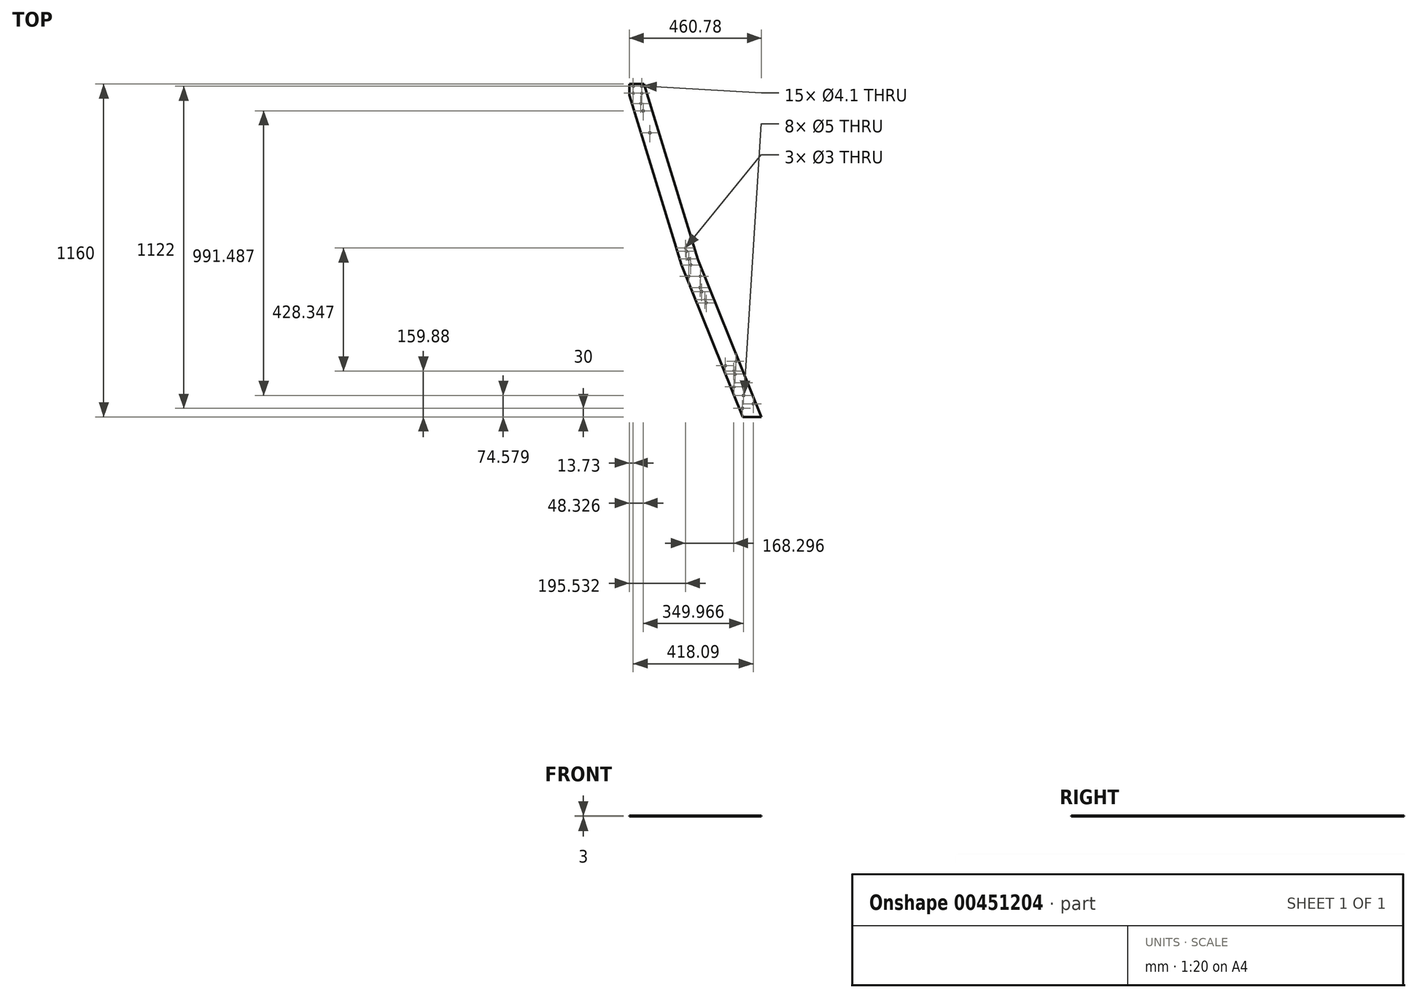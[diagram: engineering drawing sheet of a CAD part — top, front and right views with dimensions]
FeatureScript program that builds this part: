
annotation { "Feature Type Name" : "Feature", "Feature Type Description" : "" }
export const myFeature = defineFeature(function(context is Context, id is Id, definition is map)
    precondition{}
    {
        {
            var Q0;
            Q0=qCreatedBy(makeId("Top.planeOp"),FACE);
            var sketch = newSketch(context, id + "F0", { "sketchPlane" : qUnion([Q0])});
            skLineSegment(sketch, "E0", {"start": v(0, 0) * mm, "end": v(-64.71, 0) * mm});
            skLineSegment(sketch, "E1", {"start": v(-472.78, 1160) * mm, "end": v(-410, 1160) * mm});
            skLineSegment(sketch, "E2", {"start": v(-472.78, 1160) * mm, "end": v(-278.24, 528.5) * mm});
            skLineSegment(sketch, "E3", {"start": v(-278.24, 528.5) * mm, "end": v(-64.71, 0) * mm});
            skLineSegment(sketch, "E4", {"start": v(0, 0) * mm, "end": v(-221.65, 548.6) * mm});
            skLineSegment(sketch, "E5", {"start": v(-410, 1160) * mm, "end": v(-221.65, 548.6) * mm});
            skLineSegment(sketch, "E6", {"start": v(-32.36, 0) * mm, "end": v(-248.68, 535.42) * mm, "construction": true});
            skCircle(sketch, "E7", {"center": v(-208.58, 436.18) * mm, "radius": 2.5 * mm});
            skLineSegment(sketch, "E8", {"start": v(-202.7, 368.24) * mm, "end": v(-55.04, 2.75) * mm, "construction": true});
            skCircle(sketch, "E9", {"center": v(-66.05, 30) * mm, "radius": 2.05 * mm});
            skCircle(sketch, "E10", {"center": v(-96.02, 104.17) * mm, "radius": 2.05 * mm});
            skCircle(sketch, "E11", {"center": v(-125.98, 178.35) * mm, "radius": 2.05 * mm});
            skCircle(sketch, "E12.MirrorC", {"center": v(-28.96, 44.98) * mm, "radius": 2.05 * mm});
            skCircle(sketch, "E13.MirrorC", {"center": v(-58.93, 119.16) * mm, "radius": 2.05 * mm});
            skCircle(sketch, "E14.MirrorC", {"center": v(-88.9, 193.33) * mm, "radius": 2.05 * mm});
            skLineSegment(sketch, "E15", {"start": v(-125.98, 178.35) * mm, "end": v(-88.9, 193.33) * mm, "construction": true});
            skLineSegment(sketch, "E16", {"start": v(-66.05, 30) * mm, "end": v(-28.96, 44.98) * mm, "construction": true});
            skCircle(sketch, "E17", {"center": v(-62.49, 74.58) * mm, "radius": 2.5 * mm});
            skPoint(sketch, "E18", {"position": v(-92.46, 148.75) * mm});
            skCircle(sketch, "E19", {"center": v(-96.95, 159.88) * mm, "radius": 1.5 * mm});
            skCircle(sketch, "E20", {"center": v(-92.46, 148.75) * mm, "radius": 2.5 * mm});
            skCircle(sketch, "E21", {"center": v(-192.85, 397.24) * mm, "radius": 2.5 * mm});
            skCircle(sketch, "E22", {"center": v(-197.35, 408.37) * mm, "radius": 1.5 * mm});
            skCircle(sketch, "E23", {"center": v(-253.47, 550) * mm, "radius": 2.5 * mm});
            skLineSegment(sketch, "E24", {"start": v(-433.64, 1134.83) * mm, "end": v(-251.34, 543.08) * mm, "construction": true});
            skLineSegment(sketch, "E25", {"start": v(-278.24, 528.5) * mm, "end": v(-221.65, 548.6) * mm, "construction": true});
            skCircle(sketch, "E26", {"center": v(-412.45, 1066.07) * mm, "radius": 2.5 * mm});
            skCircle(sketch, "E27", {"center": v(-261.72, 576.76) * mm, "radius": 2.5 * mm});
            skCircle(sketch, "E28", {"center": v(-265.25, 588.23) * mm, "radius": 1.5 * mm});
            skCircle(sketch, "E29", {"center": v(-420.4, 1091.87) * mm, "radius": 2.05 * mm});
            skCircle(sketch, "E30", {"center": v(-388.9, 989.61) * mm, "radius": 2.5 * mm});
            skCircle(sketch, "E31", {"center": v(-246.25, 529.4) * mm, "radius": 2.05 * mm});
            skCircle(sketch, "E32", {"center": v(-214.4, 450.6) * mm, "radius": 2.05 * mm});
            skSolve(sketch);
        }
        {
            var Q0;
            Q0=qSketchRegion(id+"F0",true);
            extrude(context, id + "F1", {"entities" : qUnion([Q0]), "depth" : 3 * mm, "offsetDistance" : 25 * mm});
        }
        {
            var Q0;
            Q0=makeQuery(id+"F1.opExtrude","CAP_FACE",FACE,{"disambiguationData":[OSD([sQuery(id+"F0.wireOp",EDGE,"E0"),sQuery(id+"F0.wireOp",EDGE,"E1"),sQuery(id+"F0.wireOp",EDGE,"E2"),sQuery(id+"F0.wireOp",EDGE,"E3"),sQuery(id+"F0.wireOp",EDGE,"E4"),sQuery(id+"F0.wireOp",EDGE,"E5"),sQuery(id+"F0.wireOp",EDGE,"gJt8cwgu-VA7b-SDAH-htXG-uJ1Z7NdRgci2"),sQuery(id+"F0.wireOp",EDGE,"seKeo64r-ZTq0-B8et-10Xg-iBB15py0T0ax"),sQuery(id+"F0.wireOp",EDGE,"dKAoz8lV-Klpz-Zx3G-pcuS-yv6v6ew4PkVc")])],"isStart":false});
            var sketch = newSketch(context, id + "F2", { "sketchPlane" : qUnion([Q0])});
            skCircle(sketch, "E33", {"center": v(-252.94, 490) * mm, "radius": 2.05 * mm});
            skCircle(sketch, "E34", {"center": v(-212.94, 490) * mm, "radius": 2.05 * mm});
            skCircle(sketch, "E35", {"center": v(-447.05, 1152) * mm, "radius": 2.05 * mm});
            skCircle(sketch, "E36", {"center": v(-417.05, 1152) * mm, "radius": 2.05 * mm});
            skCircle(sketch, "E37", {"center": v(-447.05, 1128) * mm, "radius": 2.05 * mm});
            skCircle(sketch, "E38", {"center": v(-417.05, 1128) * mm, "radius": 2.05 * mm});
            skSolve(sketch);
        }
        {
            var Q0;
            Q0 = qSketchRegion(id + "F2", true);
            extrude(context, id + "F3", {"entities" : qUnion([Q0]), "operationType" : NewBodyOperationType.REMOVE, "oppositeDirection" : true, "depth" : 25 * mm, "offsetDistance" : 25 * mm});
        }
        {
            var Q0;
            Q0=makeQuery(id+"F1.opExtrude","CAP_FACE",FACE,{"disambiguationData":[OSD([sQuery(id+"F0.wireOp",EDGE,"E0"),sQuery(id+"F0.wireOp",EDGE,"E1"),sQuery(id+"F0.wireOp",EDGE,"E2"),sQuery(id+"F0.wireOp",EDGE,"E3"),sQuery(id+"F0.wireOp",EDGE,"E4"),sQuery(id+"F0.wireOp",EDGE,"E5"),sQuery(id+"F0.wireOp",EDGE,"E7"),sQuery(id+"F0.wireOp",EDGE,"E9"),sQuery(id+"F0.wireOp",EDGE,"E10"),sQuery(id+"F0.wireOp",EDGE,"E11"),sQuery(id+"F0.wireOp",EDGE,"E12.MirrorC"),sQuery(id+"F0.wireOp",EDGE,"E13.MirrorC"),sQuery(id+"F0.wireOp",EDGE,"E14.MirrorC"),sQuery(id+"F0.wireOp",EDGE,"E17"),sQuery(id+"F0.wireOp",EDGE,"E19"),sQuery(id+"F0.wireOp",EDGE,"E20"),sQuery(id+"F0.wireOp",EDGE,"E21"),sQuery(id+"F0.wireOp",EDGE,"E22"),sQuery(id+"F0.wireOp",EDGE,"E23"),sQuery(id+"F0.wireOp",EDGE,"E26"),sQuery(id+"F0.wireOp",EDGE,"E27"),sQuery(id+"F0.wireOp",EDGE,"E28"),sQuery(id+"F0.wireOp",EDGE,"E29"),sQuery(id+"F0.wireOp",EDGE,"E30")])],"isStart":false});
            var sketch = newSketch(context, id + "F4", { "sketchPlane" : qUnion([Q0])});
            skLineSegment(sketch, "E39", {"start": v(-460.78, 1160) * mm, "end": v(-460.78, 1121.05) * mm});
            skLineSegment(sketch, "E40", {"start": v(-460.78, 1121.05) * mm, "end": v(-472.78, 1160) * mm});
            skLineSegment(sketch, "E41", {"start": v(-472.78, 1160) * mm, "end": v(-460.78, 1160) * mm});
            skSolve(sketch);
        }
        {
            var Q0;
            Q0 = qSketchRegion(id + "F4", true);
            extrude(context, id + "F5", {"entities" : qUnion([Q0]), "operationType" : NewBodyOperationType.REMOVE, "oppositeDirection" : true, "depth" : 25 * mm, "offsetDistance" : 25 * mm});
        }
    });
